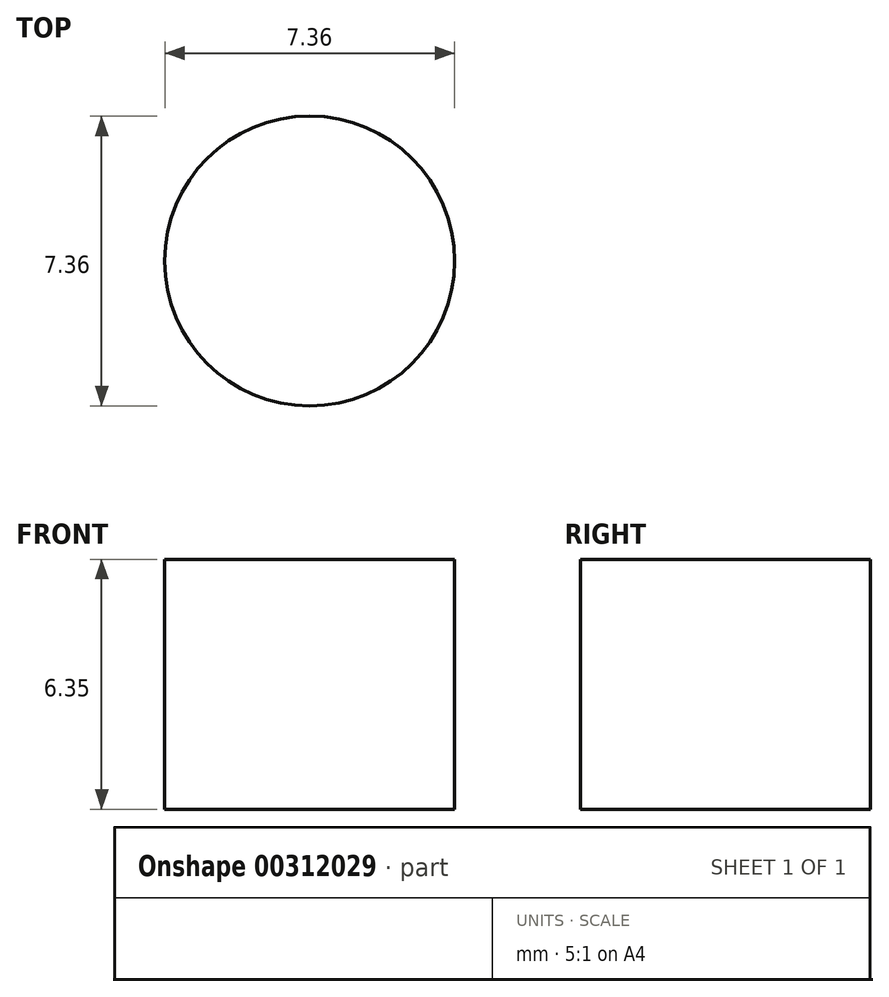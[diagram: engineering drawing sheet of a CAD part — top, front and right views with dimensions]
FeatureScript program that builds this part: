
annotation { "Feature Type Name" : "Feature", "Feature Type Description" : "" }
export const myFeature = defineFeature(function(context is Context, id is Id, definition is map)
    precondition{}
    {
        {
            var Q0;
            Q0=qCreatedBy(makeId("Top.planeOp"),FACE);
            var sketch = newSketch(context, id + "F0", { "sketchPlane" : qUnion([Q0])});
            skCircle(sketch, "E0", {"center": v(0, 0) * mm, "radius": 3.68 * mm});
            skSolve(sketch);
        }
        {
            var Q0;
            Q0 = qSketchRegion(id + "F0", true);
            extrude(context, id + "F1", {"entities" : qUnion([Q0]), "depth" : 6.35 * mm, "offsetDistance" : 25.4 * mm});
        }
    });
